# Revit family: Kal_A3-Aluminium-Sliding-Single
name_source: partatom
category: Doors
revit_build: Autodesk Revit 2016 (Build: 20150220_1215(x64)
units: mm (PartAtom-declared; Revit-internal decimal feet)

## family parameters
Always vertical = Yes
Cut with Voids When Loaded = No
Host = Wall
Room Calculation Point = No
Shared = No

## types (5) — shared parameters
Construction Type = Aluminium
Frame Finish = Anodised Aluminium
Function = Interior
Height = 2125 mm
Manufacturer = Kal-Aluminium
Material Door Frame = Default Aluminium Door Frame
Material Glass = Glass
Model = Arcadia Patio Doors
Model Type = Single Sliding
URL = http://www.kal.co.za
Wall Closure = By host
zero-valued in all types: Rough Height, Rough Width, Thickness

## per-type parameters (varying)
| type | Manufacturer Code | Width |
| 1500w X 2100h | 1500 FS | 1500 mm  [stored 4.92126 ft] |
| 1800w X 2100h | 1800 FS | 1800 mm  [stored 5.90551 ft] |
| 2100w X 2100h | 2100 FS | 2100 mm |
| 2400h X 2100h | 2400 FS | 2400 mm |
| 3000h X 2100h | 3000 FS | 3000 mm  [stored 9.84252 ft] |

note: [stored X ft] marks values corroborated as IEEE doubles in the binary element streams (Revit-internal decimal feet)

## geometry (parser evidence)
native form markers: Sweep x6
no freeform markers — native parametric forms only
